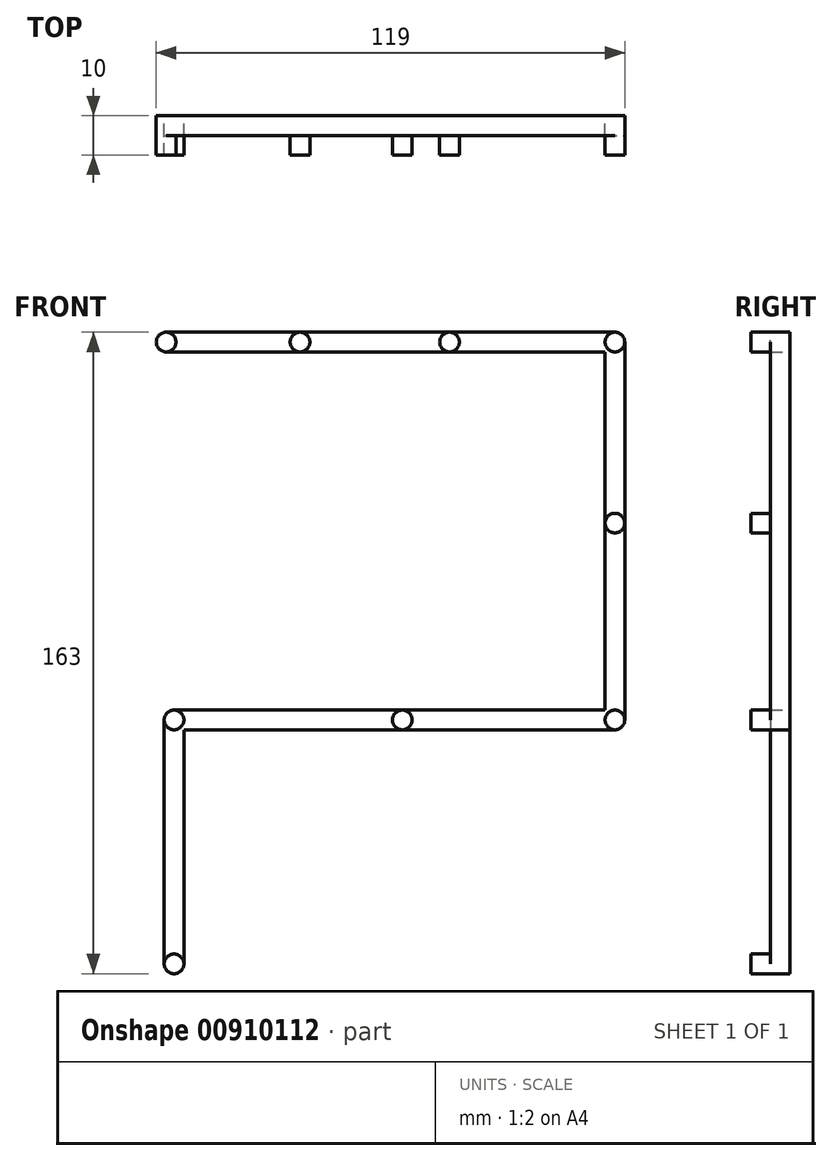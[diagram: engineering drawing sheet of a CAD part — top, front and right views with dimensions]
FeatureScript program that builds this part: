
annotation { "Feature Type Name" : "Feature", "Feature Type Description" : "" }
export const myFeature = defineFeature(function(context is Context, id is Id, definition is map)
    precondition{}
    {
        {
            var Q0;
            Q0=qCreatedBy(makeId("Front.planeOp"),FACE);
            var sketch = newSketch(context, id + "F0", { "sketchPlane" : qUnion([Q0])});
            skCircle(sketch, "E0", {"center": v(0, 0) * mm, "radius": 2.5 * mm});
            skCircle(sketch, "E1", {"center": v(34, 0) * mm, "radius": 2.5 * mm});
            skLineSegment(sketch, "E2.bottom", {"start": v(0, 2.5) * mm, "end": v(34, 2.5) * mm});
            skLineSegment(sketch, "E2.top", {"start": v(0, -2.5) * mm, "end": v(34, -2.5) * mm});
            skLineSegment(sketch, "E2.left", {"start": v(0, 2.5) * mm, "end": v(0, -2.5) * mm});
            skLineSegment(sketch, "E2.right", {"start": v(34, 2.5) * mm, "end": v(34, -2.5) * mm});
            skCircle(sketch, "E3", {"center": v(72, 0) * mm, "radius": 2.5 * mm});
            skCircle(sketch, "E4", {"center": v(114, 0) * mm, "radius": 2.5 * mm});
            skCircle(sketch, "E5", {"center": v(114, -46) * mm, "radius": 2.5 * mm});
            skCircle(sketch, "E6", {"center": v(114, -96) * mm, "radius": 2.5 * mm});
            skCircle(sketch, "E7", {"center": v(60, -96) * mm, "radius": 2.5 * mm});
            skCircle(sketch, "E8", {"center": v(2, -96) * mm, "radius": 2.5 * mm});
            skCircle(sketch, "E9", {"center": v(2, -158) * mm, "radius": 2.5 * mm});
            skLineSegment(sketch, "E10.bottom", {"start": v(34, 2.5) * mm, "end": v(72, 2.5) * mm});
            skLineSegment(sketch, "E10.top", {"start": v(34, -2.5) * mm, "end": v(72, -2.5) * mm});
            skLineSegment(sketch, "E10.right", {"start": v(72, 2.5) * mm, "end": v(72, -2.5) * mm});
            skLineSegment(sketch, "E11.bottom", {"start": v(-0.5, -96) * mm, "end": v(4.5, -96) * mm});
            skLineSegment(sketch, "E11.top", {"start": v(-0.5, -158) * mm, "end": v(4.5, -158) * mm});
            skLineSegment(sketch, "E11.left", {"start": v(-0.5, -96) * mm, "end": v(-0.5, -158) * mm});
            skLineSegment(sketch, "E11.right", {"start": v(4.5, -96) * mm, "end": v(4.5, -158) * mm});
            skLineSegment(sketch, "E12.bottom", {"start": v(2, -93.5) * mm, "end": v(60, -93.5) * mm});
            skLineSegment(sketch, "E12.top", {"start": v(2, -98.5) * mm, "end": v(60, -98.5) * mm});
            skLineSegment(sketch, "E12.left", {"start": v(2, -93.5) * mm, "end": v(2, -98.5) * mm});
            skLineSegment(sketch, "E12.right", {"start": v(60, -93.5) * mm, "end": v(60, -98.5) * mm});
            skLineSegment(sketch, "E13.bottom", {"start": v(60, -93.5) * mm, "end": v(114, -93.5) * mm});
            skLineSegment(sketch, "E13.top", {"start": v(60, -98.5) * mm, "end": v(114, -98.5) * mm});
            skLineSegment(sketch, "E13.right", {"start": v(114, -93.5) * mm, "end": v(114, -98.5) * mm});
            skLineSegment(sketch, "E14.bottom", {"start": v(111.5, 0) * mm, "end": v(116.5, 0) * mm});
            skLineSegment(sketch, "E14.top", {"start": v(111.5, -96) * mm, "end": v(116.5, -96) * mm});
            skLineSegment(sketch, "E14.left", {"start": v(111.5, 0) * mm, "end": v(111.5, -96) * mm});
            skLineSegment(sketch, "E14.right", {"start": v(116.5, 0) * mm, "end": v(116.5, -96) * mm});
            skLineSegment(sketch, "E15.bottom", {"start": v(72, 2.5) * mm, "end": v(114, 2.5) * mm});
            skLineSegment(sketch, "E15.top", {"start": v(72, -2.5) * mm, "end": v(114, -2.5) * mm});
            skLineSegment(sketch, "E15.right", {"start": v(114, 2.5) * mm, "end": v(114, -2.5) * mm});
            skSolve(sketch);
        }
        {
            var Q0;
            {var subQ0=sQuery(id+"F0.wireOp",EDGE,"E2.left");Q0=makeQuery(id+"F0.imprint","IMPRINT",FACE,{"disambiguationData":[TD([[makeQuery(id+"F0.imprint","IMPRINT",EDGE,{"derivedFrom":subQ0}),1.0]])]});}
            var Q1;
            {var subQ0=sQuery(id+"F0.wireOp",EDGE,"E2.left");Q1=makeQuery(id+"F0.imprint","IMPRINT",FACE,{"disambiguationData":[TD([[makeQuery(id+"F0.imprint","IMPRINT",EDGE,{"derivedFrom":subQ0}),-1.0]])]});}
            var Q2;
            {var subQ0=sQuery(id+"F0.wireOp",EDGE,"E2.right");Q2=makeQuery(id+"F0.imprint","IMPRINT",FACE,{"disambiguationData":[TD([[makeQuery(id+"F0.imprint","IMPRINT",EDGE,{"derivedFrom":subQ0}),1.0]])]});}
            var Q3;
            {var subQ0=sQuery(id+"F0.wireOp",EDGE,"E2.right");Q3=makeQuery(id+"F0.imprint","IMPRINT",FACE,{"disambiguationData":[TD([[makeQuery(id+"F0.imprint","IMPRINT",EDGE,{"derivedFrom":subQ0}),-1.0]])]});}
            var Q4;
            {var subQ0=sQuery(id+"F0.wireOp",EDGE,"E14.bottom");var subQ3=sQuery(id+"F0.wireOp",EDGE,"E15.right");var subQ5=makeQuery(id+"F0.imprint","INTERSECT",VERTEX,{"derivedFrom":[subQ0,subQ3]});Q4=makeQuery(id+"F0.imprint","IMPRINT",FACE,{"disambiguationData":[TD([[makeQuery(id+"F0.imprint","IMPRINT",EDGE,{"disambiguationData":[TD([[subQ5,-1.0]])],"derivedFrom":subQ0}),-1.0]])]});}
            var Q5;
            {var subQ0=sQuery(id+"F0.wireOp",EDGE,"E14.bottom");var subQ3=sQuery(id+"F0.wireOp",EDGE,"E15.right");var subQ5=makeQuery(id+"F0.imprint","INTERSECT",VERTEX,{"derivedFrom":[subQ0,subQ3]});Q5=makeQuery(id+"F0.imprint","IMPRINT",FACE,{"disambiguationData":[TD([[makeQuery(id+"F0.imprint","IMPRINT",EDGE,{"disambiguationData":[TD([[subQ5,-1.0]])],"derivedFrom":subQ0}),1.0]])]});}
            var Q6;
            {var subQ0=sQuery(id+"F0.wireOp",EDGE,"E14.bottom");var subQ3=sQuery(id+"F0.wireOp",EDGE,"E15.right");var subQ5=makeQuery(id+"F0.imprint","INTERSECT",VERTEX,{"derivedFrom":[subQ0,subQ3]});Q6=makeQuery(id+"F0.imprint","IMPRINT",FACE,{"disambiguationData":[TD([[makeQuery(id+"F0.imprint","IMPRINT",EDGE,{"disambiguationData":[TD([[subQ5,1.0]])],"derivedFrom":subQ0}),1.0]])]});}
            var Q7;
            {var subQ0=sQuery(id+"F0.wireOp",EDGE,"E10.right");Q7=makeQuery(id+"F0.imprint","IMPRINT",FACE,{"disambiguationData":[TD([[makeQuery(id+"F0.imprint","IMPRINT",EDGE,{"derivedFrom":subQ0}),-1.0]])]});}
            var Q8;
            {var subQ0=sQuery(id+"F0.wireOp",EDGE,"E10.right");Q8=makeQuery(id+"F0.imprint","IMPRINT",FACE,{"disambiguationData":[TD([[makeQuery(id+"F0.imprint","IMPRINT",EDGE,{"derivedFrom":subQ0}),1.0]])]});}
            var Q9;
            {var subQ0=sQuery(id+"F0.wireOp",EDGE,"E14.bottom");var subQ3=sQuery(id+"F0.wireOp",EDGE,"E15.right");var subQ5=makeQuery(id+"F0.imprint","INTERSECT",VERTEX,{"derivedFrom":[subQ0,subQ3]});Q9=makeQuery(id+"F0.imprint","IMPRINT",FACE,{"disambiguationData":[TD([[makeQuery(id+"F0.imprint","IMPRINT",EDGE,{"disambiguationData":[TD([[subQ5,1.0]])],"derivedFrom":subQ0}),-1.0]])]});}
            var Q10;
            {var subQ0=sQuery(id+"F0.wireOp",EDGE,"E5");var subQ1=makeQuery(id+"F0.imprint","INTERSECT",VERTEX,{"derivedFrom":[subQ0,sQuery(id+"F0.wireOp",EDGE,"E14.left")]});Q10=makeQuery(id+"F0.imprint","IMPRINT",FACE,{"disambiguationData":[TD([[makeQuery(id+"F0.imprint","IMPRINT",EDGE,{"disambiguationData":[TD([[subQ1,1.0]])],"derivedFrom":subQ0}),1.0]])]});}
            var Q11;
            {var subQ0=sQuery(id+"F0.wireOp",EDGE,"E13.right");var subQ3=sQuery(id+"F0.wireOp",EDGE,"E14.top");var subQ5=makeQuery(id+"F0.imprint","INTERSECT",VERTEX,{"derivedFrom":[subQ0,subQ3]});Q11=makeQuery(id+"F0.imprint","IMPRINT",FACE,{"disambiguationData":[TD([[makeQuery(id+"F0.imprint","IMPRINT",EDGE,{"disambiguationData":[TD([[subQ5,1.0]])],"derivedFrom":subQ0}),1.0]])]});}
            var Q12;
            {var subQ0=sQuery(id+"F0.wireOp",EDGE,"E13.right");var subQ3=sQuery(id+"F0.wireOp",EDGE,"E14.top");var subQ5=makeQuery(id+"F0.imprint","INTERSECT",VERTEX,{"derivedFrom":[subQ0,subQ3]});Q12=makeQuery(id+"F0.imprint","IMPRINT",FACE,{"disambiguationData":[TD([[makeQuery(id+"F0.imprint","IMPRINT",EDGE,{"disambiguationData":[TD([[subQ5,-1.0]])],"derivedFrom":subQ0}),-1.0]])]});}
            var Q13;
            {var subQ0=sQuery(id+"F0.wireOp",EDGE,"E13.right");var subQ3=sQuery(id+"F0.wireOp",EDGE,"E14.top");var subQ5=makeQuery(id+"F0.imprint","INTERSECT",VERTEX,{"derivedFrom":[subQ0,subQ3]});Q13=makeQuery(id+"F0.imprint","IMPRINT",FACE,{"disambiguationData":[TD([[makeQuery(id+"F0.imprint","IMPRINT",EDGE,{"disambiguationData":[TD([[subQ5,-1.0]])],"derivedFrom":subQ0}),1.0]])]});}
            var Q14;
            {var subQ0=sQuery(id+"F0.wireOp",EDGE,"E13.right");var subQ3=sQuery(id+"F0.wireOp",EDGE,"E14.top");var subQ5=makeQuery(id+"F0.imprint","INTERSECT",VERTEX,{"derivedFrom":[subQ0,subQ3]});Q14=makeQuery(id+"F0.imprint","IMPRINT",FACE,{"disambiguationData":[TD([[makeQuery(id+"F0.imprint","IMPRINT",EDGE,{"disambiguationData":[TD([[subQ5,1.0]])],"derivedFrom":subQ0}),-1.0]])]});}
            var Q15;
            {var subQ0=sQuery(id+"F0.wireOp",EDGE,"E12.right");Q15=makeQuery(id+"F0.imprint","IMPRINT",FACE,{"disambiguationData":[TD([[makeQuery(id+"F0.imprint","IMPRINT",EDGE,{"derivedFrom":subQ0}),1.0]])]});}
            var Q16;
            {var subQ0=sQuery(id+"F0.wireOp",EDGE,"E12.right");Q16=makeQuery(id+"F0.imprint","IMPRINT",FACE,{"disambiguationData":[TD([[makeQuery(id+"F0.imprint","IMPRINT",EDGE,{"derivedFrom":subQ0}),-1.0]])]});}
            var Q17;
            {var subQ0=sQuery(id+"F0.wireOp",EDGE,"E11.bottom");var subQ3=sQuery(id+"F0.wireOp",EDGE,"E12.left");var subQ5=makeQuery(id+"F0.imprint","INTERSECT",VERTEX,{"derivedFrom":[subQ0,subQ3]});Q17=makeQuery(id+"F0.imprint","IMPRINT",FACE,{"disambiguationData":[TD([[makeQuery(id+"F0.imprint","IMPRINT",EDGE,{"disambiguationData":[TD([[subQ5,-1.0]])],"derivedFrom":subQ0}),-1.0]])]});}
            var Q18;
            {var subQ0=sQuery(id+"F0.wireOp",EDGE,"E11.bottom");var subQ3=sQuery(id+"F0.wireOp",EDGE,"E12.left");var subQ5=makeQuery(id+"F0.imprint","INTERSECT",VERTEX,{"derivedFrom":[subQ0,subQ3]});Q18=makeQuery(id+"F0.imprint","IMPRINT",FACE,{"disambiguationData":[TD([[makeQuery(id+"F0.imprint","IMPRINT",EDGE,{"disambiguationData":[TD([[subQ5,1.0]])],"derivedFrom":subQ0}),-1.0]])]});}
            var Q19;
            {var subQ0=sQuery(id+"F0.wireOp",EDGE,"E11.bottom");var subQ3=sQuery(id+"F0.wireOp",EDGE,"E12.left");var subQ5=makeQuery(id+"F0.imprint","INTERSECT",VERTEX,{"derivedFrom":[subQ0,subQ3]});Q19=makeQuery(id+"F0.imprint","IMPRINT",FACE,{"disambiguationData":[TD([[makeQuery(id+"F0.imprint","IMPRINT",EDGE,{"disambiguationData":[TD([[subQ5,1.0]])],"derivedFrom":subQ0}),1.0]])]});}
            var Q20;
            {var subQ0=sQuery(id+"F0.wireOp",EDGE,"E11.bottom");var subQ3=sQuery(id+"F0.wireOp",EDGE,"E12.left");var subQ5=makeQuery(id+"F0.imprint","INTERSECT",VERTEX,{"derivedFrom":[subQ0,subQ3]});Q20=makeQuery(id+"F0.imprint","IMPRINT",FACE,{"disambiguationData":[TD([[makeQuery(id+"F0.imprint","IMPRINT",EDGE,{"disambiguationData":[TD([[subQ5,-1.0]])],"derivedFrom":subQ0}),1.0]])]});}
            var Q21;
            {var subQ0=sQuery(id+"F0.wireOp",EDGE,"E11.top");Q21=makeQuery(id+"F0.imprint","IMPRINT",FACE,{"disambiguationData":[TD([[makeQuery(id+"F0.imprint","IMPRINT",EDGE,{"derivedFrom":subQ0}),-1.0]])]});}
            var Q22;
            {var subQ0=sQuery(id+"F0.wireOp",EDGE,"E11.top");Q22=makeQuery(id+"F0.imprint","IMPRINT",FACE,{"disambiguationData":[TD([[makeQuery(id+"F0.imprint","IMPRINT",EDGE,{"derivedFrom":subQ0}),1.0]])]});}
            extrude(context, id + "F1", {"entities" : qUnion([Q0, Q1, Q2, Q3, Q4, Q5, Q6, Q7, Q8, Q9, Q10, Q11, Q12, Q13, Q14, Q15, Q16, Q17, Q18, Q19, Q20, Q21, Q22]), "depth" : 10 * mm, "offsetDistance" : 25 * mm});
        }
        {
            var Q0;
            {var subQ1=sQuery(id+"F0.wireOp",EDGE,"E2.bottom");Q0=makeQuery(id+"F0.imprint","IMPRINT",FACE,{"disambiguationData":[TD([[makeQuery(id+"F0.imprint","IMPRINT",EDGE,{"derivedFrom":subQ1}),-1.0]])]});}
            var Q1;
            {var subQ1=sQuery(id+"F0.wireOp",EDGE,"E10.bottom");Q1=makeQuery(id+"F0.imprint","IMPRINT",FACE,{"disambiguationData":[TD([[makeQuery(id+"F0.imprint","IMPRINT",EDGE,{"derivedFrom":subQ1}),-1.0]])]});}
            var Q2;
            {var subQ3=sQuery(id+"F0.wireOp",EDGE,"E5");var subQ5=sQuery(id+"F0.wireOp",EDGE,"E14.left");var subQ6=makeQuery(id+"F0.imprint","INTERSECT",VERTEX,{"derivedFrom":[subQ3,subQ5]});Q2=makeQuery(id+"F0.imprint","IMPRINT",FACE,{"disambiguationData":[TD([[makeQuery(id+"F0.imprint","IMPRINT",EDGE,{"disambiguationData":[TD([[subQ6,1.0]])],"derivedFrom":subQ3}),-1.0]])]});}
            var Q3;
            {var subQ0=sQuery(id+"F0.wireOp",EDGE,"E15.bottom");Q3=makeQuery(id+"F0.imprint","IMPRINT",FACE,{"disambiguationData":[TD([[makeQuery(id+"F0.imprint","IMPRINT",EDGE,{"derivedFrom":subQ0}),-1.0]])]});}
            var Q4;
            {var subQ0=sQuery(id+"F0.wireOp",EDGE,"E14.left");var subQ1=sQuery(id+"F0.wireOp",EDGE,"E5");var subQ2=makeQuery(id+"F0.imprint","INTERSECT",VERTEX,{"derivedFrom":[subQ1,subQ0]});Q4=makeQuery(id+"F0.imprint","IMPRINT",FACE,{"disambiguationData":[TD([[makeQuery(id+"F0.imprint","IMPRINT",EDGE,{"disambiguationData":[TD([[subQ2,-1.0]])],"derivedFrom":subQ1}),-1.0]])]});}
            var Q5;
            {var subQ0=sQuery(id+"F0.wireOp",EDGE,"E13.top");Q5=makeQuery(id+"F0.imprint","IMPRINT",FACE,{"disambiguationData":[TD([[makeQuery(id+"F0.imprint","IMPRINT",EDGE,{"derivedFrom":subQ0}),1.0]])]});}
            var Q6;
            {var subQ0=sQuery(id+"F0.wireOp",EDGE,"E12.bottom");Q6=makeQuery(id+"F0.imprint","IMPRINT",FACE,{"disambiguationData":[TD([[makeQuery(id+"F0.imprint","IMPRINT",EDGE,{"derivedFrom":subQ0}),-1.0]])]});}
            var Q7;
            {var subQ6=sQuery(id+"F0.wireOp",EDGE,"E11.left");Q7=makeQuery(id+"F0.imprint","IMPRINT",FACE,{"disambiguationData":[TD([[makeQuery(id+"F0.imprint","IMPRINT",EDGE,{"derivedFrom":subQ6}),1.0]])]});}
            var Q8;
            {var subQ0=sQuery(id+"F0.wireOp",EDGE,"E11.right");var subQ3=sQuery(id+"F0.wireOp",EDGE,"E12.top");var subQ5=makeQuery(id+"F0.imprint","INTERSECT",VERTEX,{"derivedFrom":[subQ0,subQ3]});Q8=makeQuery(id+"F0.imprint","IMPRINT",FACE,{"disambiguationData":[TD([[makeQuery(id+"F0.imprint","IMPRINT",EDGE,{"disambiguationData":[TD([[subQ5,1.0]])],"derivedFrom":subQ0}),-1.0]])]});}
            var Q9;
            {var subQ0=sQuery(id+"F0.wireOp",EDGE,"E14.left");var subQ3=sQuery(id+"F0.wireOp",EDGE,"E15.top");var subQ5=makeQuery(id+"F0.imprint","INTERSECT",VERTEX,{"derivedFrom":[subQ0,subQ3]});Q9=makeQuery(id+"F0.imprint","IMPRINT",FACE,{"disambiguationData":[TD([[makeQuery(id+"F0.imprint","IMPRINT",EDGE,{"disambiguationData":[TD([[subQ5,1.0]])],"derivedFrom":subQ0}),1.0]])]});}
            var Q10;
            {var subQ0=sQuery(id+"F0.wireOp",EDGE,"E13.bottom");var subQ3=sQuery(id+"F0.wireOp",EDGE,"E14.left");var subQ5=makeQuery(id+"F0.imprint","INTERSECT",VERTEX,{"derivedFrom":[subQ0,subQ3]});Q10=makeQuery(id+"F0.imprint","IMPRINT",FACE,{"disambiguationData":[TD([[makeQuery(id+"F0.imprint","IMPRINT",EDGE,{"disambiguationData":[TD([[subQ5,-1.0]])],"derivedFrom":subQ0}),-1.0]])]});}
            extrude(context, id + "F2", {"entities" : qUnion([Q0, Q1, Q2, Q3, Q4, Q5, Q6, Q7, Q8, Q9, Q10]), "operationType" : NewBodyOperationType.ADD, "depth" : 5 * mm, "offsetDistance" : 25 * mm});
        }
    });
